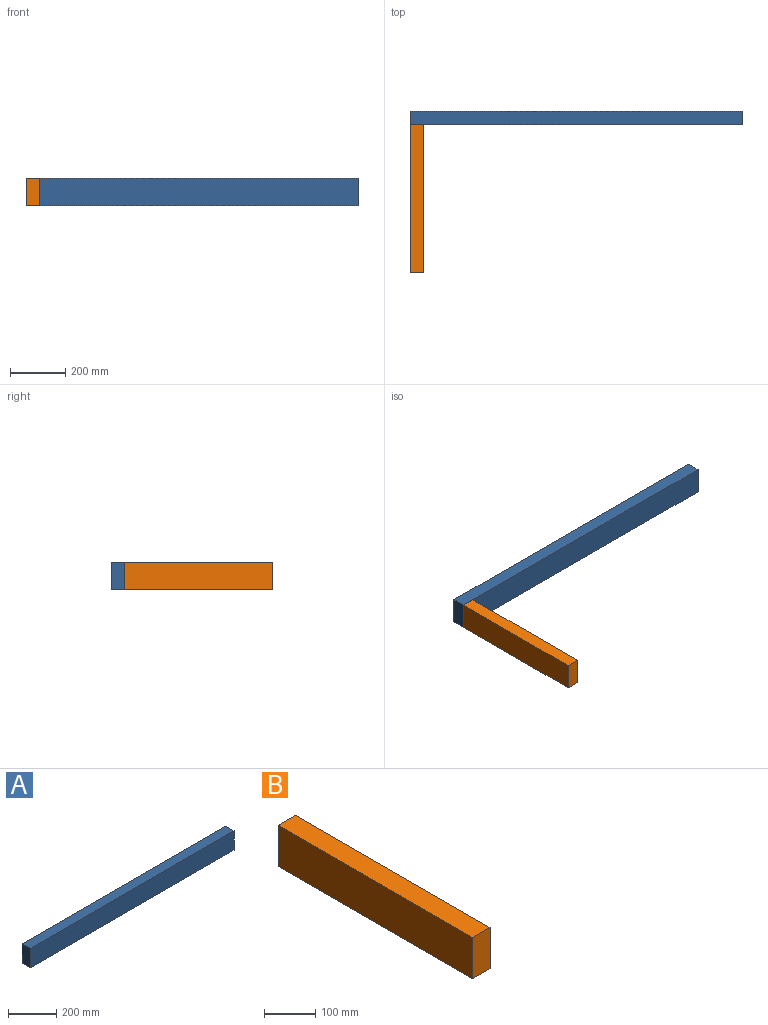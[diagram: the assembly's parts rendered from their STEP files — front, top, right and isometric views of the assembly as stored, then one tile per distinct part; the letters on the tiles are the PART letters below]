
ASSEMBLY  parts=2 mates=1
PART A: 6 faces, bbox 1200x48x98 mm
  f0: plane 1200x48mm, normal (0,0,-1), area 57600mm2, adj f1,f3,f4,f5
  f1: plane 1200x98mm, normal (0,1,0), area 117600mm2, adj f0,f2,f4,f5
  f2: plane 1200x48mm, normal (0,0,1), area 57600mm2, adj f1,f3,f4,f5
  f3: plane 1200x98mm, normal (0,-1,0), area 117600mm2, adj f0,f2,f4,f5
  f4: plane 98x48mm, normal (1,0,0), area 4704mm2, adj f0,f1,f2,f3
  f5: plane 98x48mm, normal (-1,0,0), area 4704mm2, adj f0,f1,f2,f3
PART B: 6 faces, bbox 48x536x98 mm
  f0: plane 536x48mm, normal (0,0,-1), area 25728mm2, adj f1,f3,f4,f5
  f1: plane 536x98mm, normal (1,0,0), area 52528mm2, adj f0,f2,f4,f5
  f2: plane 536x48mm, normal (0,0,1), area 25728mm2, adj f1,f3,f4,f5
  f3: plane 536x98mm, normal (-1,0,0), area 52528mm2, adj f0,f2,f4,f5
  f4: plane 98x48mm, normal (0,-1,0), area 4704mm2, adj f0,f1,f2,f3
  f5: plane 98x48mm, normal (0,1,0), area 4704mm2, adj f0,f1,f2,f3
PLACE A t=(197.11,563.24,-137.73)mm
PLACE B t=(245.11,515.24,-137.73)mm
MATE planar B.f5 <-> A.f3  axis (0,1,0) through (197.11,515.24,-39.73)mm
